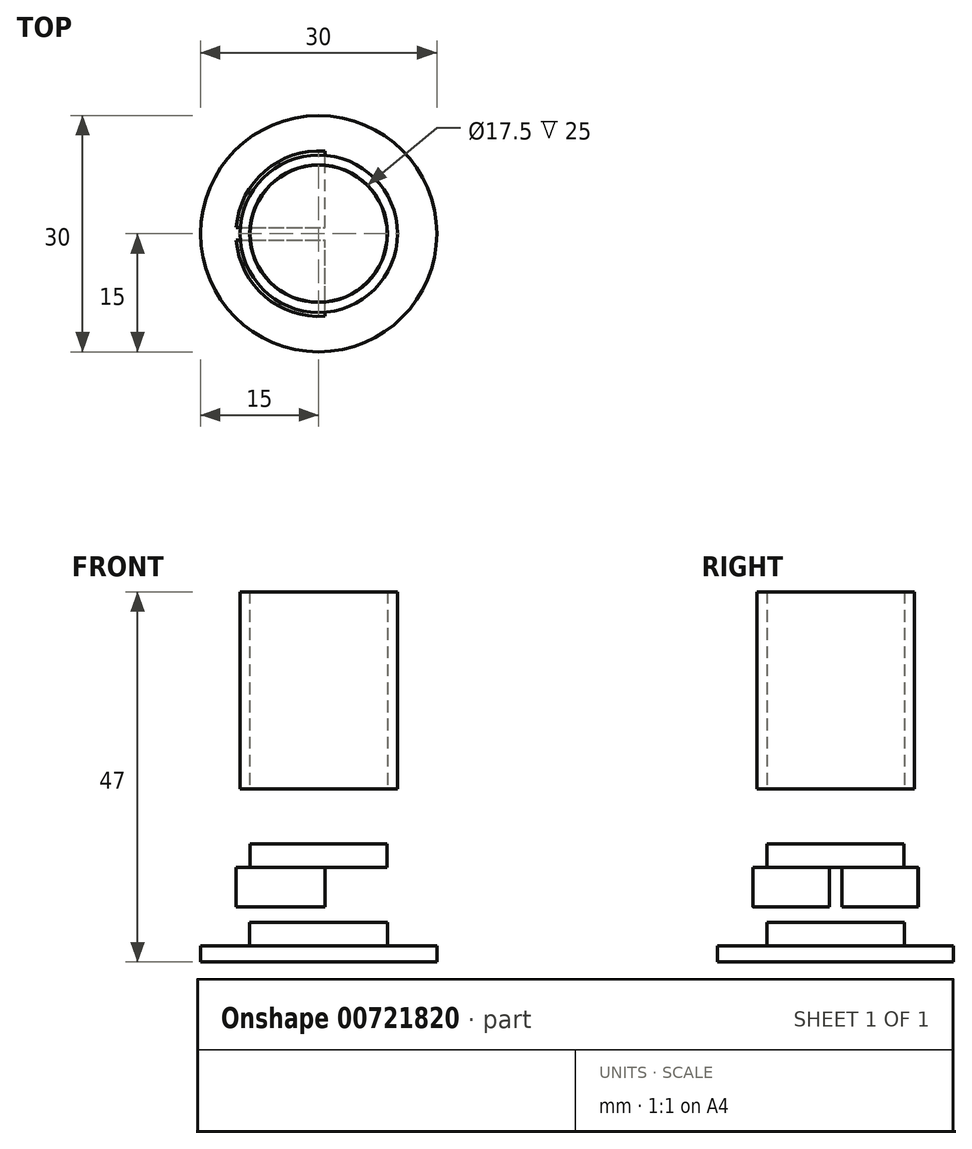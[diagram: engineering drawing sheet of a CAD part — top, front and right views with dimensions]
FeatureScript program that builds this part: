
annotation { "Feature Type Name" : "Feature", "Feature Type Description" : "" }
export const myFeature = defineFeature(function(context is Context, id is Id, definition is map)
    precondition{}
    {
        {
            var Q0;
            Q0=qCreatedBy(makeId("Top.planeOp"),FACE);
            var sketch = newSketch(context, id + "F0", { "sketchPlane" : qUnion([Q0])});
            skCircle(sketch, "E0", {"center": v(0, 0) * mm, "radius": 8.75 * mm});
            skCircle(sketch, "E1", {"center": v(0, 0) * mm, "radius": 10 * mm});
            skSolve(sketch);
        }
        {
            var Q0;
            Q0=qSketchRegion(id+"F0",true);
            extrude(context, id + "F1", {"entities" : qUnion([Q0]), "depth" : 25 * mm, "offsetDistance" : 25 * mm});
        }
        {
            var Q0;
            Q0=makeQuery(id+"F1.opExtrude","CAP_FACE",FACE,{"disambiguationData":[OSD([sQuery(id+"F0.wireOp",EDGE,"E0")])],"isStart":true});
            cPlane(context, id + "F2", {"entities" : qUnion([Q0]), "cplaneType" : CPlaneType.OFFSET, "offset" : 10 * mm, "width" : 150 * mm, "height" : 150 * mm});
        }
        {
            var Q0;
            Q0=qCreatedBy(id+"F2.planeOp",FACE);
            var sketch = newSketch(context, id + "F3", { "sketchPlane" : qUnion([Q0])});
            skCircle(sketch, "E2", {"center": v(0, 0) * mm, "radius": 8.7 * mm});
            skSolve(sketch);
        }
        {
            var Q0;
            Q0=qSketchRegion(id+"F3",true);
            extrude(context, id + "F4", {"entities" : qUnion([Q0]), "oppositeDirection" : true, "depth" : 3 * mm, "offsetDistance" : 25 * mm});
        }
        {
            var Q0;
            Q0=qCreatedBy(id+"F2.planeOp",FACE);
            var sketch = newSketch(context, id + "F5", { "sketchPlane" : qUnion([Q0])});
            skCircle(sketch, "E3.0", {"center": v(0, 0) * mm, "radius": 10.5 * mm});
            skLineSegment(sketch, "E4.bottom", {"start": v(-11.4, 0.8) * mm, "end": v(11.4, 0.8) * mm});
            skLineSegment(sketch, "E4.top", {"start": v(-11.4, -0.8) * mm, "end": v(11.4, -0.8) * mm});
            skLineSegment(sketch, "E4.left", {"start": v(-11.4, 0.8) * mm, "end": v(-11.4, -0.8) * mm});
            skLineSegment(sketch, "E4.right", {"start": v(11.4, 0.8) * mm, "end": v(11.4, -0.8) * mm});
            skLineSegment(sketch, "E5.bottom", {"start": v(-0.8, 11.11) * mm, "end": v(0.8, 11.11) * mm});
            skLineSegment(sketch, "E5.top", {"start": v(-0.8, -11.11) * mm, "end": v(0.8, -11.11) * mm});
            skLineSegment(sketch, "E5.left", {"start": v(-0.8, 11.11) * mm, "end": v(-0.8, -11.11) * mm});
            skLineSegment(sketch, "E5.right", {"start": v(0.8, 11.11) * mm, "end": v(0.8, -11.11) * mm});
            skSolve(sketch);
        }
        {
            var Q0;
            {var subQ0=sQuery(id+"F5.wireOp",EDGE,"E5.left");var subQ1=sQuery(id+"F5.wireOp",EDGE,"E3.0");var subQ2=makeQuery(id+"F5.imprint","INTERSECT",VERTEX,{"disambiguationData":[OD(0.0)],"derivedFrom":[subQ1,subQ0]});Q0=makeQuery(id+"F5.imprint","IMPRINT",FACE,{"disambiguationData":[TD([[makeQuery(id+"F5.imprint","IMPRINT",EDGE,{"disambiguationData":[TD([[subQ2,-1.0]])],"derivedFrom":subQ1}),1.0]])]});}
            var Q1;
            {var subQ0=sQuery(id+"F5.wireOp",EDGE,"E5.right");var subQ1=sQuery(id+"F5.wireOp",EDGE,"E3.0");var subQ2=makeQuery(id+"F5.imprint","INTERSECT",VERTEX,{"disambiguationData":[OD(0.0)],"derivedFrom":[subQ1,subQ0]});Q1=makeQuery(id+"F5.imprint","IMPRINT",FACE,{"disambiguationData":[TD([[makeQuery(id+"F5.imprint","IMPRINT",EDGE,{"disambiguationData":[TD([[subQ2,1.0]])],"derivedFrom":subQ1}),1.0]])]});}
            var Q2;
            {var subQ0=sQuery(id+"F5.wireOp",EDGE,"E4.top");var subQ1=sQuery(id+"F5.wireOp",EDGE,"E3.0");var subQ2=makeQuery(id+"F5.imprint","INTERSECT",VERTEX,{"disambiguationData":[OD(0.0)],"derivedFrom":[subQ1,subQ0]});Q2=makeQuery(id+"F5.imprint","IMPRINT",FACE,{"disambiguationData":[TD([[makeQuery(id+"F5.imprint","IMPRINT",EDGE,{"disambiguationData":[TD([[subQ2,-1.0]])],"derivedFrom":subQ1}),1.0]])]});}
            var Q3;
            {var subQ0=sQuery(id+"F5.wireOp",EDGE,"E5.right");var subQ1=sQuery(id+"F5.wireOp",EDGE,"E3.0");var subQ2=makeQuery(id+"F5.imprint","INTERSECT",VERTEX,{"disambiguationData":[OD(1.0)],"derivedFrom":[subQ1,subQ0]});Q3=makeQuery(id+"F5.imprint","IMPRINT",FACE,{"disambiguationData":[TD([[makeQuery(id+"F5.imprint","IMPRINT",EDGE,{"disambiguationData":[TD([[subQ2,-1.0]])],"derivedFrom":subQ1}),1.0]])]});}
            extrude(context, id + "F6", {"entities" : qUnion([Q0, Q1, Q2, Q3]), "operationType" : NewBodyOperationType.ADD, "depth" : 5 * mm, "offsetDistance" : 25 * mm});
        }
        {
            var Q0;
            Q0=qCreatedBy(makeId("Top.planeOp"),FACE);
            cPlane(context, id + "F7", {"entities" : qUnion([Q0]), "cplaneType" : CPlaneType.OFFSET, "offset" : 20 * mm, "oppositeDirection" : true, "width" : 150 * mm, "height" : 150 * mm});
        }
        {
            var Q0;
            Q0=qCreatedBy(id+"F7.planeOp",FACE);
            var sketch = newSketch(context, id + "F8", { "sketchPlane" : qUnion([Q0])});
            skCircle(sketch, "E6", {"center": v(0, 0) * mm, "radius": 8.75 * mm});
            skCircle(sketch, "E7.0", {"center": v(0, 0) * mm, "radius": 15 * mm});
            skSolve(sketch);
        }
        {
            var Q0;
            Q0=makeQuery(id+"F8.imprint","IMPRINT",FACE,{"disambiguationData":[TD([[makeQuery(id+"F8.imprint","IMPRINT",EDGE,{"derivedFrom":sQuery(id+"F8.wireOp",EDGE,"E6")}),1.0]])]});
            extrude(context, id + "F9", {"entities" : qUnion([Q0]), "depth" : 3 * mm, "offsetDistance" : 25 * mm});
        }
        {
            var Q0;
            Q0=makeQuery(id+"F8.imprint","IMPRINT",FACE,{"disambiguationData":[TD([[makeQuery(id+"F8.imprint","IMPRINT",EDGE,{"derivedFrom":sQuery(id+"F8.wireOp",EDGE,"E6")}),1.0]])]});
            var Q1;
            Q1=makeQuery(id+"F8.imprint","IMPRINT",FACE,{"disambiguationData":[TD([[makeQuery(id+"F8.imprint","IMPRINT",EDGE,{"derivedFrom":sQuery(id+"F8.wireOp",EDGE,"E6")}),-1.0]])]});
            extrude(context, id + "F10", {"entities" : qUnion([Q0, Q1]), "operationType" : NewBodyOperationType.ADD, "oppositeDirection" : true, "depth" : 2 * mm, "offsetDistance" : 25 * mm});
        }
    });
